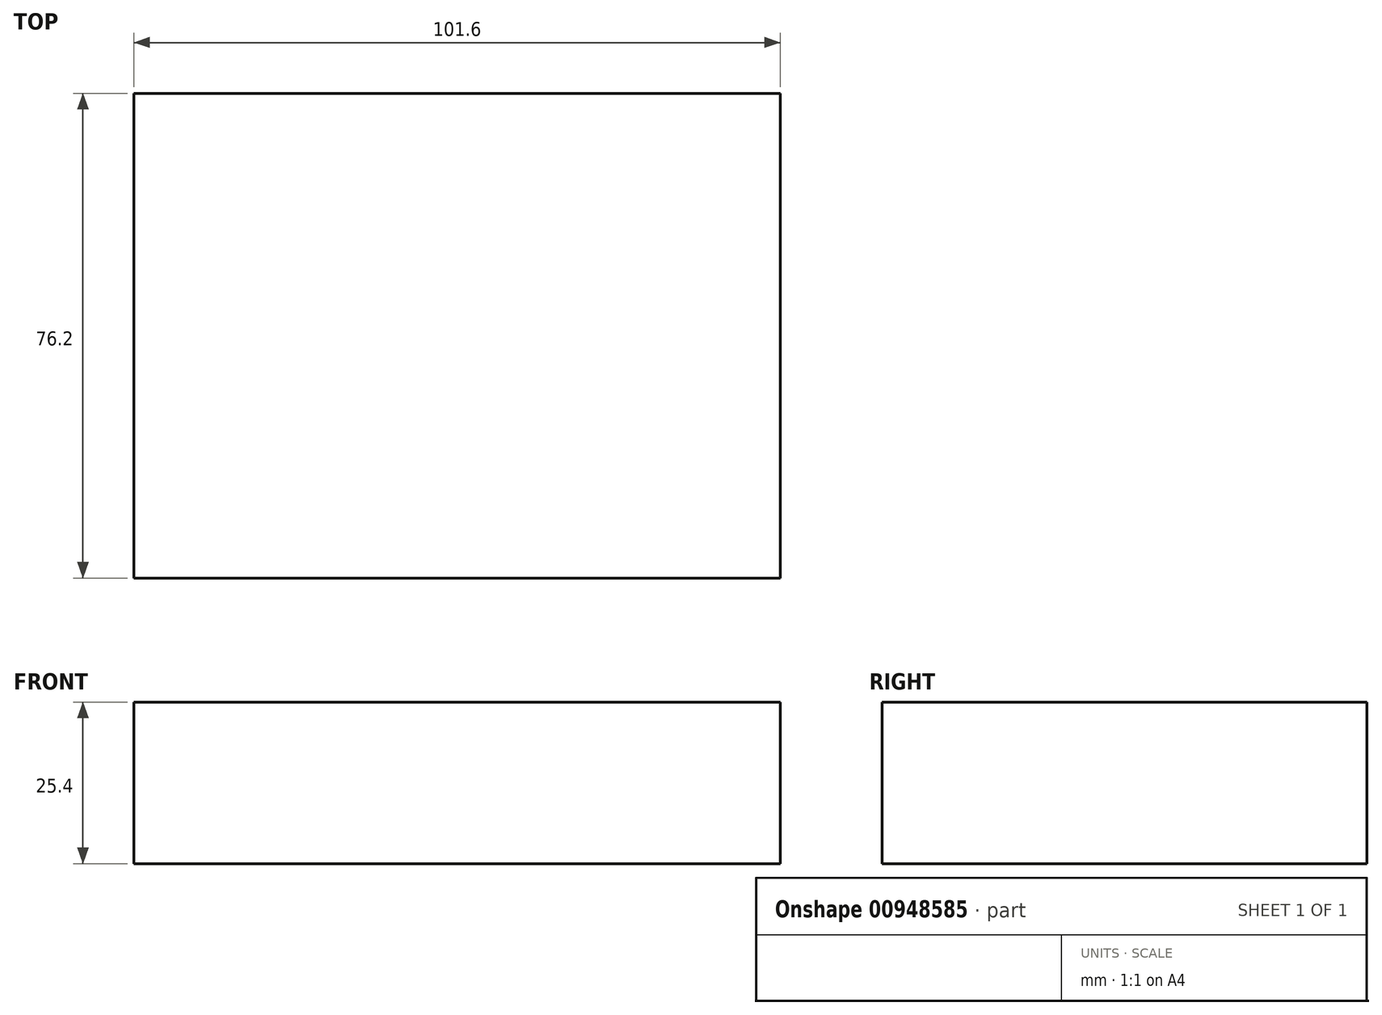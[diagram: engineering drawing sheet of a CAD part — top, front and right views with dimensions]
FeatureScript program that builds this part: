
annotation { "Feature Type Name" : "Feature", "Feature Type Description" : "" }
export const myFeature = defineFeature(function(context is Context, id is Id, definition is map)
    precondition{}
    {
        {
            var Q0;
            Q0=qCreatedBy(makeId("Top.planeOp"),FACE);
            var sketch = newSketch(context, id + "F0", { "sketchPlane" : qUnion([Q0])});
            skLineSegment(sketch, "E0.bottom", {"start": v(50.8, 38.1) * mm, "end": v(-50.8, 38.1) * mm});
            skLineSegment(sketch, "E0.top", {"start": v(50.8, -38.1) * mm, "end": v(-50.8, -38.1) * mm});
            skLineSegment(sketch, "E0.left", {"start": v(50.8, 38.1) * mm, "end": v(50.8, -38.1) * mm});
            skLineSegment(sketch, "E0.right", {"start": v(-50.8, 38.1) * mm, "end": v(-50.8, -38.1) * mm});
            skPoint(sketch, "E0.middle", {"position": v(0, 0) * mm});
            skSolve(sketch);
        }
        {
            var Q0;
            Q0 = qSketchRegion(id + "F0", true);
            extrude(context, id + "F1", {"entities" : qUnion([Q0]), "oppositeDirection" : true, "depth" : 25.4 * mm, "offsetDistance" : 25.4 * mm});
        }
    });
